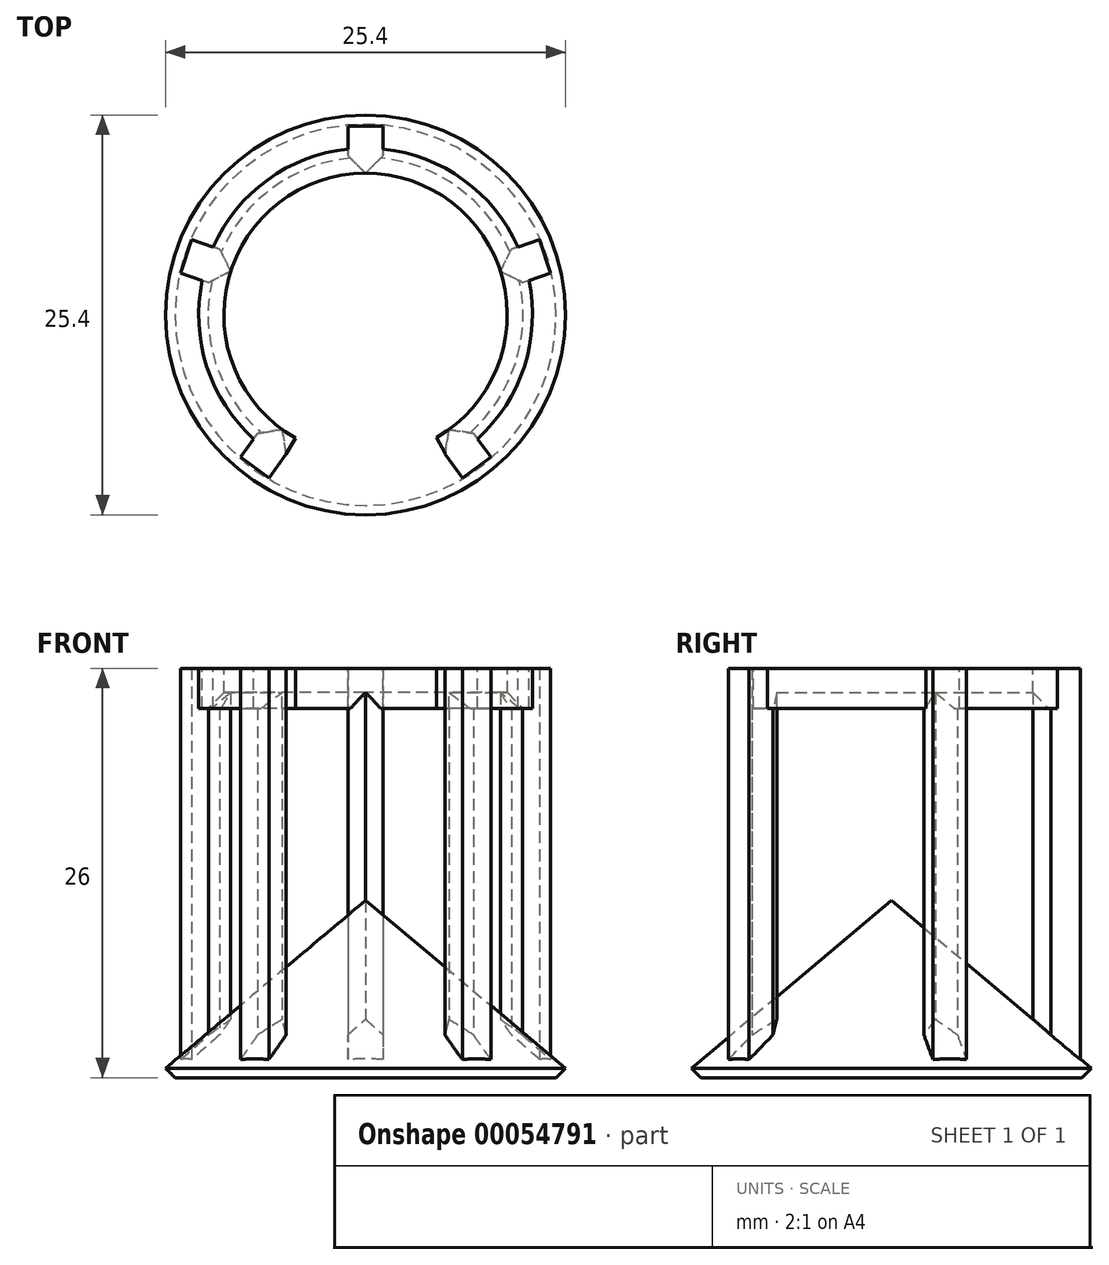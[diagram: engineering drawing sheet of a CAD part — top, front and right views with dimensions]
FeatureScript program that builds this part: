
annotation { "Feature Type Name" : "Feature", "Feature Type Description" : "" }
export const myFeature = defineFeature(function(context is Context, id is Id, definition is map)
    precondition{}
    {
        {
            var Q0;
            Q0=qCreatedBy(makeId("Front.planeOp"),FACE);
            var sketch = newSketch(context, id + "F0", { "sketchPlane" : qUnion([Q0])});
            skLineSegment(sketch, "E0", {"start": v(0, 0) * mm, "end": v(12.7, 0) * mm});
            skLineSegment(sketch, "E1", {"start": v(12.7, 0) * mm, "end": v(0, 10.66) * mm});
            skLineSegment(sketch, "E2", {"start": v(0, 10.66) * mm, "end": v(0, 0) * mm});
            skLineSegment(sketch, "E3", {"start": v(0, 10.66) * mm, "end": v(0, 39.23) * mm, "construction": true});
            skSolve(sketch);
        }
        {
            var Q0;
            Q0=makeQuery(id+"F0.imprint","IMPRINT",FACE,{"disambiguationData":[TD([[makeQuery(id+"F0.imprint","IMPRINT",EDGE,{"derivedFrom":sQuery(id+"F0.wireOp",EDGE,"E0")}),1.0]])]});
            var Q1;
            Q1=sQuery(id+"F0.wireOp",EDGE,"E3");
            revolve(context, id + "F1", {"entities" : qUnion([Q0]), "axis" : qUnion([Q1]), "revolveType" : RevolveType.FULL});
        }
        {
            var Q0;
            Q0=qCreatedBy(makeId("Top.planeOp"),FACE);
            var sketch = newSketch(context, id + "F2", { "sketchPlane" : qUnion([Q0])});
            skCircle(sketch, "E4", {"center": v(0, 0) * mm, "radius": 9 * mm, "construction": true});
            skLineSegment(sketch, "E5", {"start": v(0, 9) * mm, "end": v(-1.12, 10.12) * mm});
            skLineSegment(sketch, "E6", {"start": v(-1.12, 10.12) * mm, "end": v(-1.12, 12) * mm});
            skLineSegment(sketch, "E7", {"start": v(-1.12, 12) * mm, "end": v(1.12, 12) * mm});
            skLineSegment(sketch, "E8", {"start": v(1.12, 12) * mm, "end": v(1.12, 10.12) * mm});
            skLineSegment(sketch, "E9", {"start": v(1.12, 10.12) * mm, "end": v(0, 9) * mm});
            skLineSegment(sketch, "E10.1.0", {"start": v(8.56, 2.78) * mm, "end": v(9.28, 4.2) * mm});
            skLineSegment(sketch, "E10.1.1", {"start": v(11.06, 4.77) * mm, "end": v(11.75, 2.64) * mm});
            skLineSegment(sketch, "E10.1.2", {"start": v(9.28, 4.2) * mm, "end": v(11.06, 4.77) * mm});
            skLineSegment(sketch, "E10.1.3", {"start": v(11.75, 2.64) * mm, "end": v(9.97, 2.06) * mm});
            skLineSegment(sketch, "E10.1.4", {"start": v(9.97, 2.06) * mm, "end": v(8.56, 2.78) * mm});
            skLineSegment(sketch, "E10.2.0", {"start": v(5.3, -7.28) * mm, "end": v(6.85, -7.53) * mm});
            skLineSegment(sketch, "E10.2.1", {"start": v(7.95, -9.04) * mm, "end": v(6.14, -10.36) * mm});
            skLineSegment(sketch, "E10.2.2", {"start": v(6.85, -7.53) * mm, "end": v(7.95, -9.04) * mm});
            skLineSegment(sketch, "E10.2.3", {"start": v(6.14, -10.36) * mm, "end": v(5.04, -8.84) * mm});
            skLineSegment(sketch, "E10.2.4", {"start": v(5.04, -8.84) * mm, "end": v(5.3, -7.28) * mm});
            skLineSegment(sketch, "E10.3.0", {"start": v(-5.3, -7.28) * mm, "end": v(-5.04, -8.84) * mm});
            skLineSegment(sketch, "E10.3.1", {"start": v(-6.14, -10.36) * mm, "end": v(-7.95, -9.04) * mm});
            skLineSegment(sketch, "E10.3.2", {"start": v(-5.04, -8.84) * mm, "end": v(-6.14, -10.36) * mm});
            skLineSegment(sketch, "E10.3.3", {"start": v(-7.95, -9.04) * mm, "end": v(-6.85, -7.53) * mm});
            skLineSegment(sketch, "E10.3.4", {"start": v(-6.85, -7.53) * mm, "end": v(-5.3, -7.28) * mm});
            skLineSegment(sketch, "E10.4.0", {"start": v(-8.56, 2.78) * mm, "end": v(-9.97, 2.06) * mm});
            skLineSegment(sketch, "E10.4.1", {"start": v(-11.75, 2.64) * mm, "end": v(-11.06, 4.77) * mm});
            skLineSegment(sketch, "E10.4.2", {"start": v(-9.97, 2.06) * mm, "end": v(-11.75, 2.64) * mm});
            skLineSegment(sketch, "E10.4.3", {"start": v(-11.06, 4.77) * mm, "end": v(-9.28, 4.2) * mm});
            skLineSegment(sketch, "E10.4.4", {"start": v(-9.28, 4.2) * mm, "end": v(-8.56, 2.78) * mm});
            skLineSegment(sketch, "E10.anchor1", {"start": v(0, 0) * mm, "end": v(0, 9) * mm, "construction": true});
            skLineSegment(sketch, "E10.anchor2", {"start": v(0, 0) * mm, "end": v(-8.56, 2.78) * mm, "construction": true});
            skSolve(sketch);
        }
        {
            var Q0;
            Q0=makeQuery(id+"F2.imprint","IMPRINT",FACE,{"disambiguationData":[TD([[makeQuery(id+"F2.imprint","IMPRINT",EDGE,{"derivedFrom":sQuery(id+"F2.wireOp",EDGE,"E10.4.0")}),-1.0]])]});
            var Q1;
            Q1=makeQuery(id+"F2.imprint","IMPRINT",FACE,{"disambiguationData":[TD([[makeQuery(id+"F2.imprint","IMPRINT",EDGE,{"derivedFrom":sQuery(id+"F2.wireOp",EDGE,"E5")}),-1.0]])]});
            var Q2;
            Q2=makeQuery(id+"F2.imprint","IMPRINT",FACE,{"disambiguationData":[TD([[makeQuery(id+"F2.imprint","IMPRINT",EDGE,{"derivedFrom":sQuery(id+"F2.wireOp",EDGE,"E10.1.0")}),-1.0]])]});
            var Q3;
            Q3=makeQuery(id+"F2.imprint","IMPRINT",FACE,{"disambiguationData":[TD([[makeQuery(id+"F2.imprint","IMPRINT",EDGE,{"derivedFrom":sQuery(id+"F2.wireOp",EDGE,"E10.2.0")}),-1.0]])]});
            var Q4;
            Q4=makeQuery(id+"F2.imprint","IMPRINT",FACE,{"disambiguationData":[TD([[makeQuery(id+"F2.imprint","IMPRINT",EDGE,{"derivedFrom":sQuery(id+"F2.wireOp",EDGE,"E10.3.0")}),-1.0]])]});
            extrude(context, id + "F3", {"entities" : qUnion([Q0, Q1, Q2, Q3, Q4]), "operationType" : NewBodyOperationType.ADD, "depth" : 25.4 * mm});
        }
        {
            var Q0;
            Q0=makeQuery(id+"F3.opExtrude","CAP_FACE",FACE,{"disambiguationData":[OSD([sQuery(id+"F2.wireOp",EDGE,"E10.3.0"),sQuery(id+"F2.wireOp",EDGE,"E10.3.1"),sQuery(id+"F2.wireOp",EDGE,"E10.3.2"),sQuery(id+"F2.wireOp",EDGE,"E10.3.3"),sQuery(id+"F2.wireOp",EDGE,"E10.3.4")])],"isStart":false});
            var sketch = newSketch(context, id + "F4", { "sketchPlane" : qUnion([Q0])});
            skCircle(sketch, "E11", {"center": v(0, 0) * mm, "radius": 9 * mm});
            skCircle(sketch, "E12", {"center": v(0, 0) * mm, "radius": 10.6 * mm});
            skLineSegment(sketch, "E13", {"start": v(0, 0) * mm, "end": v(5.3, -9.19) * mm});
            skLineSegment(sketch, "E14", {"start": v(0, 0) * mm, "end": v(-5.04, -8.84) * mm});
            skSolve(sketch);
        }
        {
            var Q0;
            Q0=makeQuery(id+"F4.imprint","IMPRINT",FACE,{"disambiguationData":[TD([[makeQuery(id+"F4.imprint","IMPRINT",EDGE,{"derivedFrom":sQuery(id+"F4.wireOp",EDGE,"E11")}),-1.0]])]});
            var Q1;
            {var subQ0=makeQuery(id+"F3.opExtrude","CAP_EDGE",EDGE,{"disambiguationData":[OSD([sQuery(id+"F2.wireOp",EDGE,"E10.3.4")])],"isStart":false});Q1=makeQuery(id+"F4.imprint","IMPRINT",FACE,{"disambiguationData":[TD([[makeQuery(id+"F4.imprint","IMPRINT",EDGE,{"derivedFrom":subQ0}),1.0]])]});}
            extrude(context, id + "F5", {"entities" : qUnion([Q0, Q1]), "operationType" : NewBodyOperationType.ADD, "oppositeDirection" : true, "depth" : 2.54 * mm});
        }
        {
            var Q0;
            Q0=makeQuery(id+"F1.opRevolve","SWEPT_FACE",FACE,{"disambiguationData":[OSD([sQuery(id+"F0.wireOp",EDGE,"E0")])]});
            extrude(context, id + "F6", {"entities" : qUnion([Q0]), "operationType" : NewBodyOperationType.ADD, "depth" : 0.6 * mm, "hasDraft" : true, "draftAngle" : 45 * degree, "draftPullDirection" : true});
        }
        {
            var Q0;
            {var subQ0=sQuery(id+"F4.wireOp",EDGE,"E11");var subQ1=sQuery(id+"F2.wireOp",EDGE,"E10.3.4");var subQ3=sQuery(id+"F4.wireOp",EDGE,"E13");var subQ4=makeQuery(id+"F4.imprint","IMPRINT",EDGE,{"disambiguationData":[TD([[makeQuery(id+"F4.imprint","INTERSECT",VERTEX,{"derivedFrom":[subQ0,subQ3]}),-1.0]])],"derivedFrom":subQ0});Q0=makeQuery(id+"F5.boolean.opBoolean","SPLIT",EDGE,{"disambiguationData":[TD([makeQuery(id+"F3.opExtrude","SWEPT_FACE",FACE,{"disambiguationData":[OSD([sQuery(id+"F2.wireOp",EDGE,"E5")])]}),makeQuery(id+"F3.opExtrude","SWEPT_FACE",FACE,{"disambiguationData":[OSD([sQuery(id+"F2.wireOp",EDGE,"E9")])]}),makeQuery(id+"F3.opExtrude","SWEPT_FACE",FACE,{"disambiguationData":[OSD([sQuery(id+"F2.wireOp",EDGE,"E10.4.0")])]}),makeQuery(id+"F3.opExtrude","SWEPT_FACE",FACE,{"disambiguationData":[OSD([sQuery(id+"F2.wireOp",EDGE,"E10.4.4")])]}),makeQuery(id+"F5.opExtrude","SWEPT_FACE",FACE,{"disambiguationData":[OSD([subQ0]),TDD([makeQuery(id+"F4.imprint","IMPRINT",EDGE,{"disambiguationData":[TD([[makeQuery(id+"F4.imprint","INTERSECT",VERTEX,{"derivedFrom":[subQ0,sQuery(id+"F4.wireOp",EDGE,"E14")]}),1.0]])],"derivedFrom":subQ0})])]}),makeQuery(id+"F5.opExtrude","SWEPT_FACE",FACE,{"disambiguationData":[OSD([subQ0]),TDD([subQ4])]}),makeQuery(id+"F5.opExtrude","CAP_FACE",FACE,{"disambiguationData":[OSD([sQuery(id+"F2.wireOp",EDGE,"E10.3.3"),subQ1,subQ0,sQuery(id+"F4.wireOp",EDGE,"E12"),subQ3])],"isStart":false})])],"derivedFrom":makeQuery(id+"F5.opExtrude","CAP_EDGE",EDGE,{"disambiguationData":[OSD([subQ0]),TDD([subQ4])],"isStart":false})});}
            var Q1;
            {var subQ0=sQuery(id+"F2.wireOp",EDGE,"E10.3.4");var subQ1=sQuery(id+"F2.wireOp",EDGE,"E10.3.0");var subQ2=sQuery(id+"F4.wireOp",EDGE,"E14");var subQ3=sQuery(id+"F4.wireOp",EDGE,"E11");var subQ4=sQuery(id+"F4.wireOp",EDGE,"E13");var subQ6=makeQuery(id+"F4.imprint","IMPRINT",EDGE,{"disambiguationData":[TD([[makeQuery(id+"F4.imprint","INTERSECT",VERTEX,{"derivedFrom":[subQ3,subQ4]}),-1.0]])],"derivedFrom":subQ3});Q1=makeQuery(id+"F5.boolean.opBoolean","SPLIT",EDGE,{"disambiguationData":[TD([makeQuery(id+"F3.opExtrude","SWEPT_FACE",FACE,{"disambiguationData":[OSD([subQ1])]}),makeQuery(id+"F3.opExtrude","SWEPT_FACE",FACE,{"disambiguationData":[OSD([subQ0])]}),makeQuery(id+"F3.opExtrude","SWEPT_FACE",FACE,{"disambiguationData":[OSD([sQuery(id+"F2.wireOp",EDGE,"E10.4.0")])]}),makeQuery(id+"F3.opExtrude","SWEPT_FACE",FACE,{"disambiguationData":[OSD([sQuery(id+"F2.wireOp",EDGE,"E10.4.4")])]}),makeQuery(id+"F5.opExtrude","SWEPT_FACE",FACE,{"disambiguationData":[OSD([subQ3]),TDD([makeQuery(id+"F4.imprint","IMPRINT",EDGE,{"disambiguationData":[TD([[makeQuery(id+"F4.imprint","INTERSECT",VERTEX,{"derivedFrom":[subQ3,subQ2]}),1.0]])],"derivedFrom":subQ3})])]}),makeQuery(id+"F5.opExtrude","CAP_FACE",FACE,{"disambiguationData":[OSD([subQ1,subQ3,subQ2])],"isStart":false}),makeQuery(id+"F5.opExtrude","SWEPT_FACE",FACE,{"disambiguationData":[OSD([subQ3]),TDD([subQ6])]}),makeQuery(id+"F5.opExtrude","CAP_FACE",FACE,{"disambiguationData":[OSD([sQuery(id+"F2.wireOp",EDGE,"E10.3.3"),subQ0,subQ3,sQuery(id+"F4.wireOp",EDGE,"E12"),subQ4])],"isStart":false})])],"derivedFrom":makeQuery(id+"F5.opExtrude","CAP_EDGE",EDGE,{"disambiguationData":[OSD([subQ3]),TDD([subQ6])],"isStart":false})});}
            var Q2;
            {var subQ0=sQuery(id+"F4.wireOp",EDGE,"E11");var subQ1=sQuery(id+"F2.wireOp",EDGE,"E10.3.4");var subQ3=sQuery(id+"F4.wireOp",EDGE,"E13");var subQ4=makeQuery(id+"F4.imprint","IMPRINT",EDGE,{"disambiguationData":[TD([[makeQuery(id+"F4.imprint","INTERSECT",VERTEX,{"derivedFrom":[subQ0,subQ3]}),-1.0]])],"derivedFrom":subQ0});Q2=makeQuery(id+"F5.boolean.opBoolean","SPLIT",EDGE,{"disambiguationData":[TD([makeQuery(id+"F3.opExtrude","SWEPT_FACE",FACE,{"disambiguationData":[OSD([sQuery(id+"F2.wireOp",EDGE,"E5")])]}),makeQuery(id+"F3.opExtrude","SWEPT_FACE",FACE,{"disambiguationData":[OSD([sQuery(id+"F2.wireOp",EDGE,"E9")])]}),makeQuery(id+"F3.opExtrude","SWEPT_FACE",FACE,{"disambiguationData":[OSD([sQuery(id+"F2.wireOp",EDGE,"E10.1.0")])]}),makeQuery(id+"F3.opExtrude","SWEPT_FACE",FACE,{"disambiguationData":[OSD([sQuery(id+"F2.wireOp",EDGE,"E10.1.4")])]}),makeQuery(id+"F5.opExtrude","SWEPT_FACE",FACE,{"disambiguationData":[OSD([subQ0]),TDD([makeQuery(id+"F4.imprint","IMPRINT",EDGE,{"disambiguationData":[TD([[makeQuery(id+"F4.imprint","INTERSECT",VERTEX,{"derivedFrom":[subQ0,sQuery(id+"F4.wireOp",EDGE,"E14")]}),1.0]])],"derivedFrom":subQ0})])]}),makeQuery(id+"F5.opExtrude","SWEPT_FACE",FACE,{"disambiguationData":[OSD([subQ0]),TDD([subQ4])]}),makeQuery(id+"F5.opExtrude","CAP_FACE",FACE,{"disambiguationData":[OSD([sQuery(id+"F2.wireOp",EDGE,"E10.3.3"),subQ1,subQ0,sQuery(id+"F4.wireOp",EDGE,"E12"),subQ3])],"isStart":false})])],"derivedFrom":makeQuery(id+"F5.opExtrude","CAP_EDGE",EDGE,{"disambiguationData":[OSD([subQ0]),TDD([subQ4])],"isStart":false})});}
            var Q3;
            {var subQ0=sQuery(id+"F4.wireOp",EDGE,"E11");var subQ1=sQuery(id+"F2.wireOp",EDGE,"E10.3.4");var subQ3=sQuery(id+"F4.wireOp",EDGE,"E13");var subQ4=makeQuery(id+"F4.imprint","IMPRINT",EDGE,{"disambiguationData":[TD([[makeQuery(id+"F4.imprint","INTERSECT",VERTEX,{"derivedFrom":[subQ0,subQ3]}),-1.0]])],"derivedFrom":subQ0});Q3=makeQuery(id+"F5.boolean.opBoolean","SPLIT",EDGE,{"disambiguationData":[TD([makeQuery(id+"F3.opExtrude","SWEPT_FACE",FACE,{"disambiguationData":[OSD([sQuery(id+"F2.wireOp",EDGE,"E10.1.0")])]}),makeQuery(id+"F3.opExtrude","SWEPT_FACE",FACE,{"disambiguationData":[OSD([sQuery(id+"F2.wireOp",EDGE,"E10.1.4")])]}),makeQuery(id+"F3.opExtrude","SWEPT_FACE",FACE,{"disambiguationData":[OSD([sQuery(id+"F2.wireOp",EDGE,"E10.2.0")])]}),makeQuery(id+"F3.opExtrude","SWEPT_FACE",FACE,{"disambiguationData":[OSD([sQuery(id+"F2.wireOp",EDGE,"E10.2.4")])]}),makeQuery(id+"F5.opExtrude","SWEPT_FACE",FACE,{"disambiguationData":[OSD([subQ0]),TDD([makeQuery(id+"F4.imprint","IMPRINT",EDGE,{"disambiguationData":[TD([[makeQuery(id+"F4.imprint","INTERSECT",VERTEX,{"derivedFrom":[subQ0,sQuery(id+"F4.wireOp",EDGE,"E14")]}),1.0]])],"derivedFrom":subQ0})])]}),makeQuery(id+"F5.opExtrude","SWEPT_FACE",FACE,{"disambiguationData":[OSD([subQ0]),TDD([subQ4])]}),makeQuery(id+"F5.opExtrude","CAP_FACE",FACE,{"disambiguationData":[OSD([sQuery(id+"F2.wireOp",EDGE,"E10.3.3"),subQ1,subQ0,sQuery(id+"F4.wireOp",EDGE,"E12"),subQ3])],"isStart":false})])],"derivedFrom":makeQuery(id+"F5.opExtrude","CAP_EDGE",EDGE,{"disambiguationData":[OSD([subQ0]),TDD([subQ4])],"isStart":false})});}
            chamfer(context, id + "F7", {"entities" : qUnion([Q0, Q1, Q2, Q3]), "width" : 1 * mm, "tangentPropagation" : true});
        }
    });
